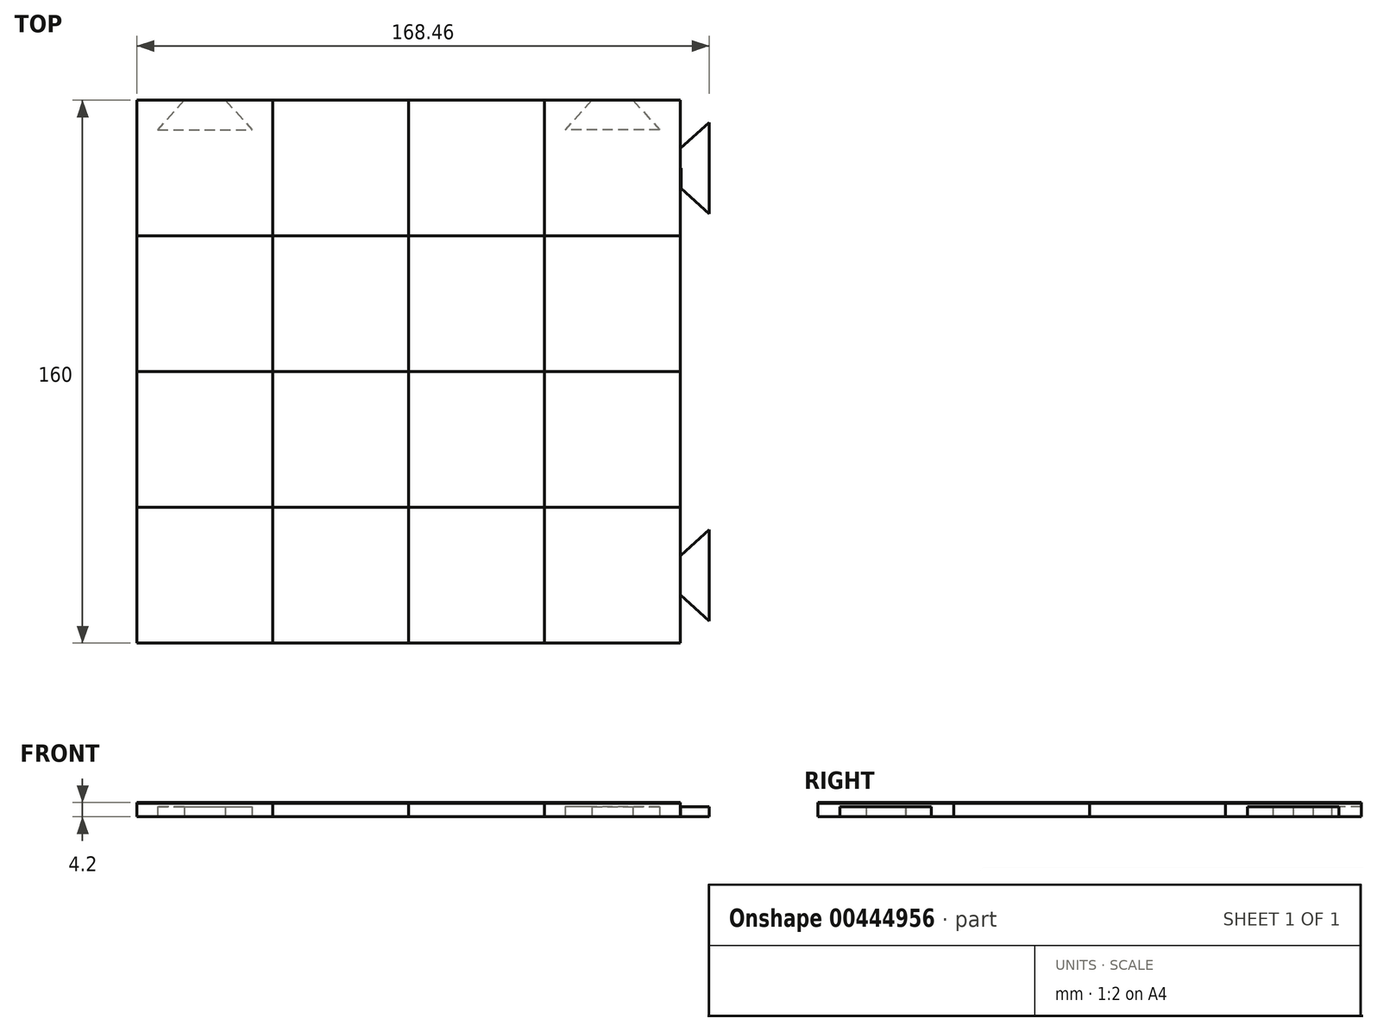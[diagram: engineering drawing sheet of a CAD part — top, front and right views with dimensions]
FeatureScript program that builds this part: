
annotation { "Feature Type Name" : "Feature", "Feature Type Description" : "" }
export const myFeature = defineFeature(function(context is Context, id is Id, definition is map)
    precondition{}
    {
        {
            var Q0;
            Q0=qCreatedBy(makeId("Top.planeOp"),FACE);
            var sketch = newSketch(context, id + "F0", { "sketchPlane" : qUnion([Q0])});
            skLineSegment(sketch, "E0.bottom", {"start": v(-80, -80) * mm, "end": v(80, -80) * mm});
            skLineSegment(sketch, "E0.top", {"start": v(-80, 80) * mm, "end": v(80, 80) * mm});
            skLineSegment(sketch, "E0.left", {"start": v(-80, -80) * mm, "end": v(-80, 80) * mm});
            skLineSegment(sketch, "E0.right", {"start": v(80, -80) * mm, "end": v(80, 80) * mm});
            skPoint(sketch, "E0.middle", {"position": v(0, 0) * mm});
            skLineSegment(sketch, "E1", {"start": v(-40, 80) * mm, "end": v(-40, -80) * mm});
            skLineSegment(sketch, "E2", {"start": v(0, 80) * mm, "end": v(0, -80) * mm});
            skLineSegment(sketch, "E3.MirrorCS", {"start": v(40, 80) * mm, "end": v(40, -80) * mm});
            skLineSegment(sketch, "E4", {"start": v(-80, 0) * mm, "end": v(80, 0) * mm});
            skLineSegment(sketch, "E5", {"start": v(-80, 40) * mm, "end": v(80, 40) * mm});
            skLineSegment(sketch, "E6.MirrorCS", {"start": v(-80, -40) * mm, "end": v(80, -40) * mm});
            skPoint(sketch, "E7.middle", {"position": v(80, 40) * mm});
            skLineSegment(sketch, "E8", {"start": v(40, 40) * mm, "end": v(80, 80) * mm});
            skLineSegment(sketch, "E9.right", {"start": v(88.66, 46.12) * mm, "end": v(88.66, 73.88) * mm});
            skPoint(sketch, "E9.middle", {"position": v(80, 60) * mm});
            skPoint(sketch, "E9.middle.positionSnap0", {"position": v(60, 60) * mm});
            skPoint(sketch, "E9.centerSnap0", {"position": v(60, 60) * mm});
            skLineSegment(sketch, "E10", {"start": v(80, 66.06) * mm, "end": v(88.66, 73.88) * mm});
            skLineSegment(sketch, "E11", {"start": v(80, 60) * mm, "end": v(88.66, 60) * mm});
            skLineSegment(sketch, "E12.MirrorCS", {"start": v(80, 53.94) * mm, "end": v(88.66, 46.12) * mm});
            skLineSegment(sketch, "E13.MirrorCS", {"start": v(80, -66.06) * mm, "end": v(88.66, -73.88) * mm});
            skLineSegment(sketch, "E14.MirrorCS", {"start": v(80, -60) * mm, "end": v(88.66, -60) * mm});
            skLineSegment(sketch, "E15.MirrorCS", {"start": v(80, -53.94) * mm, "end": v(88.66, -46.12) * mm});
            skLineSegment(sketch, "E16.MirrorCS", {"start": v(88.66, -46.12) * mm, "end": v(88.66, -73.88) * mm});
            skLineSegment(sketch, "E17.MirrorCS", {"start": v(73.88, 71.34) * mm, "end": v(46.12, 71.34) * mm});
            skLineSegment(sketch, "E18.MirrorCS", {"start": v(66.06, 80) * mm, "end": v(73.88, 71.34) * mm});
            skLineSegment(sketch, "E19.MirrorCS", {"start": v(60, 80) * mm, "end": v(60, 71.34) * mm});
            skLineSegment(sketch, "E20.MirrorCS", {"start": v(53.94, 80) * mm, "end": v(46.12, 71.34) * mm});
            skLineSegment(sketch, "E21.MirrorCS", {"start": v(-73.88, 71.34) * mm, "end": v(-46.12, 71.34) * mm});
            skLineSegment(sketch, "E22.MirrorCS", {"start": v(-66.06, 80) * mm, "end": v(-73.88, 71.34) * mm});
            skLineSegment(sketch, "E23.MirrorCS", {"start": v(-60, 80) * mm, "end": v(-60, 71.34) * mm});
            skLineSegment(sketch, "E24.MirrorCS", {"start": v(-53.94, 80) * mm, "end": v(-46.12, 71.34) * mm});
            skLineSegment(sketch, "E25", {"start": v(-66.06, 80) * mm, "end": v(-53.94, 80) * mm});
            skLineSegment(sketch, "E26", {"start": v(80, 66.06) * mm, "end": v(80, 53.94) * mm});
            skLineSegment(sketch, "E27.0", {"start": v(80.2, 65.97) * mm, "end": v(88.46, 73.43) * mm});
            skLineSegment(sketch, "E27.1", {"start": v(80.2, 65.97) * mm, "end": v(80.2, 54.03) * mm});
            skLineSegment(sketch, "E27.2", {"start": v(80.2, 54.03) * mm, "end": v(88.46, 46.57) * mm});
            skLineSegment(sketch, "E27.3", {"start": v(88.46, 46.57) * mm, "end": v(88.46, 73.43) * mm});
            skLineSegment(sketch, "E28", {"start": v(80.2, 65.97) * mm, "end": v(80, 65.79) * mm});
            skLineSegment(sketch, "E29", {"start": v(80.2, 54.03) * mm, "end": v(80, 54.2) * mm});
            skLineSegment(sketch, "E30.MirrorCS", {"start": v(80.2, -54.03) * mm, "end": v(80, -54.2) * mm});
            skLineSegment(sketch, "E31.MirrorCS", {"start": v(80.2, -65.97) * mm, "end": v(80, -65.79) * mm});
            skLineSegment(sketch, "E32.MirrorCS", {"start": v(80.2, -54.03) * mm, "end": v(88.46, -46.57) * mm});
            skLineSegment(sketch, "E33.MirrorCS", {"start": v(80.2, -65.97) * mm, "end": v(88.46, -73.43) * mm});
            skLineSegment(sketch, "E34.MirrorCS", {"start": v(88.46, -46.57) * mm, "end": v(88.46, -73.43) * mm});
            skSolve(sketch);
        }
        {
            var Q0;
            {var subQ9=sQuery(id+"F0.wireOp",EDGE,"E22.MirrorCS");Q0=makeQuery(id+"F0.imprint","IMPRINT",FACE,{"disambiguationData":[TD([[makeQuery(id+"F0.imprint","IMPRINT",EDGE,{"derivedFrom":subQ9}),-1.0]])]});}
            var Q1;
            {var subQ0=sQuery(id+"F0.wireOp",EDGE,"E22.MirrorCS");Q1=makeQuery(id+"F0.imprint","IMPRINT",FACE,{"disambiguationData":[TD([[makeQuery(id+"F0.imprint","IMPRINT",EDGE,{"derivedFrom":subQ0}),1.0]])]});}
            var Q2;
            {var subQ2=sQuery(id+"F0.wireOp",EDGE,"E23.MirrorCS");Q2=makeQuery(id+"F0.imprint","IMPRINT",FACE,{"disambiguationData":[TD([[makeQuery(id+"F0.imprint","IMPRINT",EDGE,{"derivedFrom":subQ2}),1.0]])]});}
            var Q3;
            {var subQ0=sQuery(id+"F0.wireOp",EDGE,"E1");var subQ1=sQuery(id+"F0.wireOp",EDGE,"E0.top");var subQ2=makeQuery(id+"F0.imprint","INTERSECT",VERTEX,{"derivedFrom":[subQ1,subQ0]});Q3=makeQuery(id+"F0.imprint","IMPRINT",FACE,{"disambiguationData":[TD([[makeQuery(id+"F0.imprint","IMPRINT",EDGE,{"disambiguationData":[TD([[subQ2,-1.0]])],"derivedFrom":subQ1}),-1.0]])]});}
            var Q4;
            {var subQ0=sQuery(id+"F0.wireOp",EDGE,"E2");var subQ1=sQuery(id+"F0.wireOp",EDGE,"E0.top");var subQ2=makeQuery(id+"F0.imprint","INTERSECT",VERTEX,{"derivedFrom":[subQ1,subQ0]});Q4=makeQuery(id+"F0.imprint","IMPRINT",FACE,{"disambiguationData":[TD([[makeQuery(id+"F0.imprint","IMPRINT",EDGE,{"disambiguationData":[TD([[subQ2,-1.0]])],"derivedFrom":subQ1}),-1.0]])]});}
            var Q5;
            {var subQ6=sQuery(id+"F0.wireOp",EDGE,"E20.MirrorCS");Q5=makeQuery(id+"F0.imprint","IMPRINT",FACE,{"disambiguationData":[TD([[makeQuery(id+"F0.imprint","IMPRINT",EDGE,{"derivedFrom":subQ6}),-1.0]])]});}
            var Q6;
            {var subQ3=sQuery(id+"F0.wireOp",EDGE,"E18.MirrorCS");var subQ4=sQuery(id+"F0.wireOp",EDGE,"E17.MirrorCS");var subQ5=makeQuery(id+"F0.imprint","INTERSECT",VERTEX,{"derivedFrom":[subQ4,subQ3]});Q6=makeQuery(id+"F0.imprint","IMPRINT",FACE,{"disambiguationData":[TD([[makeQuery(id+"F0.imprint","IMPRINT",EDGE,{"disambiguationData":[TD([[subQ5,-1.0]])],"derivedFrom":subQ4}),1.0]])]});}
            var Q7;
            {var subQ0=sQuery(id+"F0.wireOp",EDGE,"E17.MirrorCS");var subQ1=sQuery(id+"F0.wireOp",EDGE,"E8");var subQ2=makeQuery(id+"F0.imprint","INTERSECT",VERTEX,{"derivedFrom":[subQ1,subQ0]});Q7=makeQuery(id+"F0.imprint","IMPRINT",FACE,{"disambiguationData":[TD([[makeQuery(id+"F0.imprint","IMPRINT",EDGE,{"disambiguationData":[TD([[subQ2,-1.0]])],"derivedFrom":subQ1}),-1.0]])]});}
            var Q8;
            {var subQ7=sQuery(id+"F0.wireOp",EDGE,"E19.MirrorCS");Q8=makeQuery(id+"F0.imprint","IMPRINT",FACE,{"disambiguationData":[TD([[makeQuery(id+"F0.imprint","IMPRINT",EDGE,{"derivedFrom":subQ7}),1.0]])]});}
            var Q9;
            {var subQ1=sQuery(id+"F0.wireOp",EDGE,"E0.top");var subQ3=sQuery(id+"F0.wireOp",EDGE,"E18.MirrorCS");var subQ4=makeQuery(id+"F0.imprint","INTERSECT",VERTEX,{"derivedFrom":[subQ1,subQ3]});Q9=makeQuery(id+"F0.imprint","IMPRINT",FACE,{"disambiguationData":[TD([[makeQuery(id+"F0.imprint","IMPRINT",EDGE,{"disambiguationData":[TD([[subQ4,-1.0]])],"derivedFrom":subQ3}),1.0]])]});}
            var Q10;
            {var subQ0=sQuery(id+"F0.wireOp",EDGE,"E19.MirrorCS");Q10=makeQuery(id+"F0.imprint","IMPRINT",FACE,{"disambiguationData":[TD([[makeQuery(id+"F0.imprint","IMPRINT",EDGE,{"derivedFrom":subQ0}),-1.0]])]});}
            var Q11;
            {var subQ0=sQuery(id+"F0.wireOp",EDGE,"E5");var subQ1=sQuery(id+"F0.wireOp",EDGE,"E2");var subQ2=makeQuery(id+"F0.imprint","INTERSECT",VERTEX,{"derivedFrom":[subQ1,subQ0]});Q11=makeQuery(id+"F0.imprint","IMPRINT",FACE,{"disambiguationData":[TD([[makeQuery(id+"F0.imprint","IMPRINT",EDGE,{"disambiguationData":[TD([[subQ2,-1.0]])],"derivedFrom":subQ1}),1.0]])]});}
            var Q12;
            {var subQ0=sQuery(id+"F0.wireOp",EDGE,"E5");var subQ1=sQuery(id+"F0.wireOp",EDGE,"E1");var subQ2=makeQuery(id+"F0.imprint","INTERSECT",VERTEX,{"derivedFrom":[subQ1,subQ0]});Q12=makeQuery(id+"F0.imprint","IMPRINT",FACE,{"disambiguationData":[TD([[makeQuery(id+"F0.imprint","IMPRINT",EDGE,{"disambiguationData":[TD([[subQ2,-1.0]])],"derivedFrom":subQ1}),1.0]])]});}
            var Q13;
            {var subQ0=sQuery(id+"F0.wireOp",EDGE,"E4");var subQ1=sQuery(id+"F0.wireOp",EDGE,"E0.left");var subQ2=makeQuery(id+"F0.imprint","INTERSECT",VERTEX,{"derivedFrom":[subQ1,subQ0]});Q13=makeQuery(id+"F0.imprint","IMPRINT",FACE,{"disambiguationData":[TD([[makeQuery(id+"F0.imprint","IMPRINT",EDGE,{"disambiguationData":[TD([[subQ2,-1.0]])],"derivedFrom":subQ1}),-1.0]])]});}
            var Q14;
            {var subQ0=sQuery(id+"F0.wireOp",EDGE,"E4");var subQ1=sQuery(id+"F0.wireOp",EDGE,"E0.left");var subQ2=makeQuery(id+"F0.imprint","INTERSECT",VERTEX,{"derivedFrom":[subQ1,subQ0]});Q14=makeQuery(id+"F0.imprint","IMPRINT",FACE,{"disambiguationData":[TD([[makeQuery(id+"F0.imprint","IMPRINT",EDGE,{"disambiguationData":[TD([[subQ2,1.0]])],"derivedFrom":subQ1}),-1.0]])]});}
            var Q15;
            {var subQ0=sQuery(id+"F0.wireOp",EDGE,"E4");var subQ1=sQuery(id+"F0.wireOp",EDGE,"E1");var subQ2=makeQuery(id+"F0.imprint","INTERSECT",VERTEX,{"derivedFrom":[subQ1,subQ0]});Q15=makeQuery(id+"F0.imprint","IMPRINT",FACE,{"disambiguationData":[TD([[makeQuery(id+"F0.imprint","IMPRINT",EDGE,{"disambiguationData":[TD([[subQ2,-1.0]])],"derivedFrom":subQ1}),1.0]])]});}
            var Q16;
            {var subQ0=sQuery(id+"F0.wireOp",EDGE,"E4");var subQ1=sQuery(id+"F0.wireOp",EDGE,"E2");var subQ2=makeQuery(id+"F0.imprint","INTERSECT",VERTEX,{"derivedFrom":[subQ1,subQ0]});Q16=makeQuery(id+"F0.imprint","IMPRINT",FACE,{"disambiguationData":[TD([[makeQuery(id+"F0.imprint","IMPRINT",EDGE,{"disambiguationData":[TD([[subQ2,-1.0]])],"derivedFrom":subQ1}),1.0]])]});}
            var Q17;
            {var subQ0=sQuery(id+"F0.wireOp",EDGE,"E4");var subQ1=sQuery(id+"F0.wireOp",EDGE,"E0.right");var subQ2=makeQuery(id+"F0.imprint","INTERSECT",VERTEX,{"derivedFrom":[subQ1,subQ0]});Q17=makeQuery(id+"F0.imprint","IMPRINT",FACE,{"disambiguationData":[TD([[makeQuery(id+"F0.imprint","IMPRINT",EDGE,{"disambiguationData":[TD([[subQ2,1.0]])],"derivedFrom":subQ1}),1.0]])]});}
            var Q18;
            {var subQ0=sQuery(id+"F0.wireOp",EDGE,"E0.right");var subQ3=sQuery(id+"F0.wireOp",EDGE,"E0.bottom");var subQ4=makeQuery(id+"F0.imprint","INTERSECT",VERTEX,{"derivedFrom":[subQ3,subQ0]});Q18=makeQuery(id+"F0.imprint","IMPRINT",FACE,{"disambiguationData":[TD([[makeQuery(id+"F0.imprint","IMPRINT",EDGE,{"disambiguationData":[TD([[subQ4,1.0]])],"derivedFrom":subQ3}),1.0]])]});}
            var Q19;
            {var subQ0=sQuery(id+"F0.wireOp",EDGE,"E2");var subQ1=sQuery(id+"F0.wireOp",EDGE,"E0.bottom");var subQ2=makeQuery(id+"F0.imprint","INTERSECT",VERTEX,{"derivedFrom":[subQ1,subQ0]});Q19=makeQuery(id+"F0.imprint","IMPRINT",FACE,{"disambiguationData":[TD([[makeQuery(id+"F0.imprint","IMPRINT",EDGE,{"disambiguationData":[TD([[subQ2,-1.0]])],"derivedFrom":subQ1}),1.0]])]});}
            var Q20;
            {var subQ0=sQuery(id+"F0.wireOp",EDGE,"E1");var subQ1=sQuery(id+"F0.wireOp",EDGE,"E0.bottom");var subQ2=makeQuery(id+"F0.imprint","INTERSECT",VERTEX,{"derivedFrom":[subQ1,subQ0]});Q20=makeQuery(id+"F0.imprint","IMPRINT",FACE,{"disambiguationData":[TD([[makeQuery(id+"F0.imprint","IMPRINT",EDGE,{"disambiguationData":[TD([[subQ2,-1.0]])],"derivedFrom":subQ1}),1.0]])]});}
            var Q21;
            {var subQ0=sQuery(id+"F0.wireOp",EDGE,"E0.left");var subQ1=sQuery(id+"F0.wireOp",EDGE,"E0.bottom");var subQ2=makeQuery(id+"F0.imprint","INTERSECT",VERTEX,{"derivedFrom":[subQ1,subQ0]});Q21=makeQuery(id+"F0.imprint","IMPRINT",FACE,{"disambiguationData":[TD([[makeQuery(id+"F0.imprint","IMPRINT",EDGE,{"disambiguationData":[TD([[subQ2,-1.0]])],"derivedFrom":subQ1}),1.0]])]});}
            var Q22;
            {var subQ0=sQuery(id+"F0.wireOp",EDGE,"E4");var subQ1=sQuery(id+"F0.wireOp",EDGE,"E0.right");var subQ2=makeQuery(id+"F0.imprint","INTERSECT",VERTEX,{"derivedFrom":[subQ1,subQ0]});Q22=makeQuery(id+"F0.imprint","IMPRINT",FACE,{"disambiguationData":[TD([[makeQuery(id+"F0.imprint","IMPRINT",EDGE,{"disambiguationData":[TD([[subQ2,-1.0]])],"derivedFrom":subQ1}),1.0]])]});}
            extrude(context, id + "F1", {"entities" : qUnion([Q0, Q1, Q2, Q3, Q4, Q5, Q6, Q7, Q8, Q9, Q10, Q11, Q12, Q13, Q14, Q15, Q16, Q17, Q18, Q19, Q20, Q21, Q22]), "depth" : 4 * mm});
        }
        {
            var Q0;
            {var subQ0=sQuery(id+"F0.wireOp",EDGE,"E0.left");var subQ1=sQuery(id+"F0.wireOp",EDGE,"E0.bottom");var subQ2=makeQuery(id+"F0.imprint","INTERSECT",VERTEX,{"derivedFrom":[subQ1,subQ0]});Q0=makeQuery(id+"F0.imprint","IMPRINT",FACE,{"disambiguationData":[TD([[makeQuery(id+"F0.imprint","IMPRINT",EDGE,{"disambiguationData":[TD([[subQ2,-1.0]])],"derivedFrom":subQ1}),1.0]])]});}
            var Q1;
            {var subQ0=sQuery(id+"F0.wireOp",EDGE,"E4");var subQ1=sQuery(id+"F0.wireOp",EDGE,"E1");var subQ2=makeQuery(id+"F0.imprint","INTERSECT",VERTEX,{"derivedFrom":[subQ1,subQ0]});Q1=makeQuery(id+"F0.imprint","IMPRINT",FACE,{"disambiguationData":[TD([[makeQuery(id+"F0.imprint","IMPRINT",EDGE,{"disambiguationData":[TD([[subQ2,-1.0]])],"derivedFrom":subQ1}),1.0]])]});}
            var Q2;
            {var subQ0=sQuery(id+"F0.wireOp",EDGE,"E4");var subQ1=sQuery(id+"F0.wireOp",EDGE,"E0.left");var subQ2=makeQuery(id+"F0.imprint","INTERSECT",VERTEX,{"derivedFrom":[subQ1,subQ0]});Q2=makeQuery(id+"F0.imprint","IMPRINT",FACE,{"disambiguationData":[TD([[makeQuery(id+"F0.imprint","IMPRINT",EDGE,{"disambiguationData":[TD([[subQ2,-1.0]])],"derivedFrom":subQ1}),-1.0]])]});}
            var Q3;
            {var subQ0=sQuery(id+"F0.wireOp",EDGE,"E1");var subQ1=sQuery(id+"F0.wireOp",EDGE,"E0.top");var subQ2=makeQuery(id+"F0.imprint","INTERSECT",VERTEX,{"derivedFrom":[subQ1,subQ0]});Q3=makeQuery(id+"F0.imprint","IMPRINT",FACE,{"disambiguationData":[TD([[makeQuery(id+"F0.imprint","IMPRINT",EDGE,{"disambiguationData":[TD([[subQ2,-1.0]])],"derivedFrom":subQ1}),-1.0]])]});}
            var Q4;
            {var subQ0=sQuery(id+"F0.wireOp",EDGE,"E5");var subQ1=sQuery(id+"F0.wireOp",EDGE,"E2");var subQ2=makeQuery(id+"F0.imprint","INTERSECT",VERTEX,{"derivedFrom":[subQ1,subQ0]});Q4=makeQuery(id+"F0.imprint","IMPRINT",FACE,{"disambiguationData":[TD([[makeQuery(id+"F0.imprint","IMPRINT",EDGE,{"disambiguationData":[TD([[subQ2,-1.0]])],"derivedFrom":subQ1}),1.0]])]});}
            var Q5;
            {var subQ0=sQuery(id+"F0.wireOp",EDGE,"E4");var subQ1=sQuery(id+"F0.wireOp",EDGE,"E0.right");var subQ2=makeQuery(id+"F0.imprint","INTERSECT",VERTEX,{"derivedFrom":[subQ1,subQ0]});Q5=makeQuery(id+"F0.imprint","IMPRINT",FACE,{"disambiguationData":[TD([[makeQuery(id+"F0.imprint","IMPRINT",EDGE,{"disambiguationData":[TD([[subQ2,1.0]])],"derivedFrom":subQ1}),1.0]])]});}
            var Q6;
            {var subQ0=sQuery(id+"F0.wireOp",EDGE,"E2");var subQ1=sQuery(id+"F0.wireOp",EDGE,"E0.bottom");var subQ2=makeQuery(id+"F0.imprint","INTERSECT",VERTEX,{"derivedFrom":[subQ1,subQ0]});Q6=makeQuery(id+"F0.imprint","IMPRINT",FACE,{"disambiguationData":[TD([[makeQuery(id+"F0.imprint","IMPRINT",EDGE,{"disambiguationData":[TD([[subQ2,-1.0]])],"derivedFrom":subQ1}),1.0]])]});}
            var Q7;
            {var subQ6=sQuery(id+"F0.wireOp",EDGE,"E20.MirrorCS");Q7=makeQuery(id+"F0.imprint","IMPRINT",FACE,{"disambiguationData":[TD([[makeQuery(id+"F0.imprint","IMPRINT",EDGE,{"derivedFrom":subQ6}),-1.0]])]});}
            var Q8;
            {var subQ3=sQuery(id+"F0.wireOp",EDGE,"E18.MirrorCS");var subQ4=sQuery(id+"F0.wireOp",EDGE,"E17.MirrorCS");var subQ5=makeQuery(id+"F0.imprint","INTERSECT",VERTEX,{"derivedFrom":[subQ4,subQ3]});Q8=makeQuery(id+"F0.imprint","IMPRINT",FACE,{"disambiguationData":[TD([[makeQuery(id+"F0.imprint","IMPRINT",EDGE,{"disambiguationData":[TD([[subQ5,-1.0]])],"derivedFrom":subQ4}),1.0]])]});}
            var Q9;
            {var subQ7=sQuery(id+"F0.wireOp",EDGE,"E19.MirrorCS");Q9=makeQuery(id+"F0.imprint","IMPRINT",FACE,{"disambiguationData":[TD([[makeQuery(id+"F0.imprint","IMPRINT",EDGE,{"derivedFrom":subQ7}),1.0]])]});}
            var Q10;
            {var subQ0=sQuery(id+"F0.wireOp",EDGE,"E19.MirrorCS");Q10=makeQuery(id+"F0.imprint","IMPRINT",FACE,{"disambiguationData":[TD([[makeQuery(id+"F0.imprint","IMPRINT",EDGE,{"derivedFrom":subQ0}),-1.0]])]});}
            var Q11;
            {var subQ1=sQuery(id+"F0.wireOp",EDGE,"E0.top");var subQ3=sQuery(id+"F0.wireOp",EDGE,"E18.MirrorCS");var subQ4=makeQuery(id+"F0.imprint","INTERSECT",VERTEX,{"derivedFrom":[subQ1,subQ3]});Q11=makeQuery(id+"F0.imprint","IMPRINT",FACE,{"disambiguationData":[TD([[makeQuery(id+"F0.imprint","IMPRINT",EDGE,{"disambiguationData":[TD([[subQ4,-1.0]])],"derivedFrom":subQ3}),1.0]])]});}
            var Q12;
            {var subQ0=sQuery(id+"F0.wireOp",EDGE,"E17.MirrorCS");var subQ1=sQuery(id+"F0.wireOp",EDGE,"E8");var subQ2=makeQuery(id+"F0.imprint","INTERSECT",VERTEX,{"derivedFrom":[subQ1,subQ0]});Q12=makeQuery(id+"F0.imprint","IMPRINT",FACE,{"disambiguationData":[TD([[makeQuery(id+"F0.imprint","IMPRINT",EDGE,{"disambiguationData":[TD([[subQ2,-1.0]])],"derivedFrom":subQ1}),-1.0]])]});}
            extrude(context, id + "F2", {"entities" : qUnion([Q0, Q1, Q2, Q3, Q4, Q5, Q6, Q7, Q8, Q9, Q10, Q11, Q12]), "depth" : 4.2 * mm});
        }
        {
            var Q0;
            {var subQ0=sQuery(id+"F0.wireOp",EDGE,"E19.MirrorCS");Q0=makeQuery(id+"F0.imprint","IMPRINT",FACE,{"disambiguationData":[TD([[makeQuery(id+"F0.imprint","IMPRINT",EDGE,{"derivedFrom":subQ0}),-1.0]])]});}
            var Q1;
            {var subQ7=sQuery(id+"F0.wireOp",EDGE,"E19.MirrorCS");Q1=makeQuery(id+"F0.imprint","IMPRINT",FACE,{"disambiguationData":[TD([[makeQuery(id+"F0.imprint","IMPRINT",EDGE,{"derivedFrom":subQ7}),1.0]])]});}
            var Q2;
            {var subQ0=sQuery(id+"F0.wireOp",EDGE,"E17.MirrorCS");var subQ1=sQuery(id+"F0.wireOp",EDGE,"E8");var subQ2=makeQuery(id+"F0.imprint","INTERSECT",VERTEX,{"derivedFrom":[subQ1,subQ0]});Q2=makeQuery(id+"F0.imprint","IMPRINT",FACE,{"disambiguationData":[TD([[makeQuery(id+"F0.imprint","IMPRINT",EDGE,{"disambiguationData":[TD([[subQ2,-1.0]])],"derivedFrom":subQ1}),-1.0]])]});}
            var Q3;
            {var subQ0=sQuery(id+"F0.wireOp",EDGE,"E22.MirrorCS");Q3=makeQuery(id+"F0.imprint","IMPRINT",FACE,{"disambiguationData":[TD([[makeQuery(id+"F0.imprint","IMPRINT",EDGE,{"derivedFrom":subQ0}),1.0]])]});}
            var Q4;
            {var subQ2=sQuery(id+"F0.wireOp",EDGE,"E23.MirrorCS");Q4=makeQuery(id+"F0.imprint","IMPRINT",FACE,{"disambiguationData":[TD([[makeQuery(id+"F0.imprint","IMPRINT",EDGE,{"derivedFrom":subQ2}),1.0]])]});}
            extrude(context, id + "F3", {"entities" : qUnion([Q0, Q1, Q2, Q3, Q4]), "operationType" : NewBodyOperationType.REMOVE, "depth" : 3 * mm});
        }
        {
            var Q0;
            {var subQ5=sQuery(id+"F0.wireOp",EDGE,"E28");Q0=makeQuery(id+"F0.imprint","IMPRINT",FACE,{"disambiguationData":[TD([[makeQuery(id+"F0.imprint","IMPRINT",EDGE,{"derivedFrom":subQ5}),1.0]])]});}
            var Q1;
            {var subQ5=sQuery(id+"F0.wireOp",EDGE,"E27.2");Q1=makeQuery(id+"F0.imprint","IMPRINT",FACE,{"disambiguationData":[TD([[makeQuery(id+"F0.imprint","IMPRINT",EDGE,{"derivedFrom":subQ5}),1.0]])]});}
            var Q2;
            {var subQ5=sQuery(id+"F0.wireOp",EDGE,"E27.0");Q2=makeQuery(id+"F0.imprint","IMPRINT",FACE,{"disambiguationData":[TD([[makeQuery(id+"F0.imprint","IMPRINT",EDGE,{"derivedFrom":subQ5}),-1.0]])]});}
            var Q3;
            {var subQ0=sQuery(id+"F0.wireOp",EDGE,"E30.MirrorCS");Q3=makeQuery(id+"F0.imprint","IMPRINT",FACE,{"disambiguationData":[TD([[makeQuery(id+"F0.imprint","IMPRINT",EDGE,{"derivedFrom":subQ0}),1.0]])]});}
            var Q4;
            {var subQ4=sQuery(id+"F0.wireOp",EDGE,"E31.MirrorCS");Q4=makeQuery(id+"F0.imprint","IMPRINT",FACE,{"disambiguationData":[TD([[makeQuery(id+"F0.imprint","IMPRINT",EDGE,{"derivedFrom":subQ4}),-1.0]])]});}
            extrude(context, id + "F4", {"entities" : qUnion([Q0, Q1, Q2, Q3, Q4]), "depth" : 3 * mm});
        }
    });
